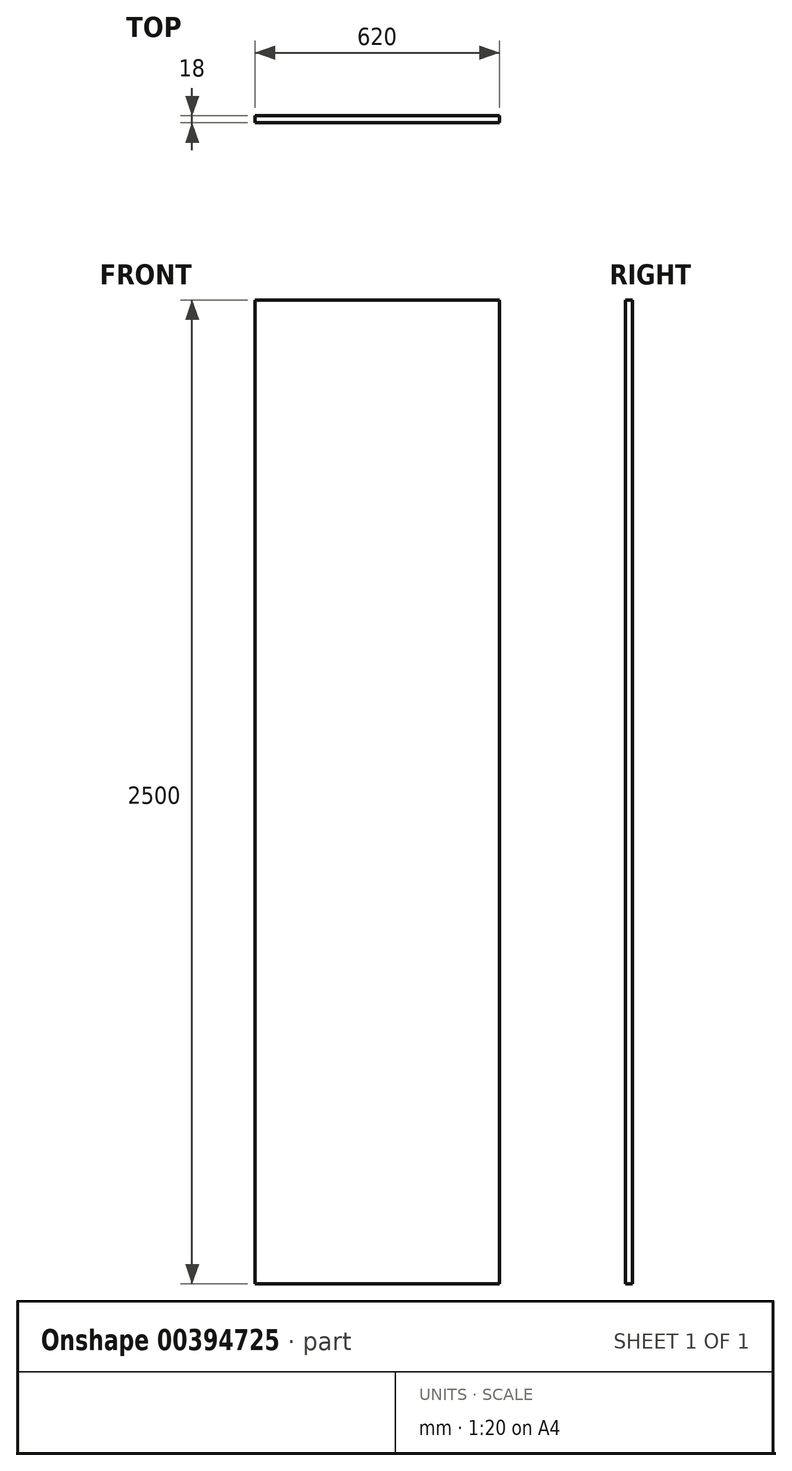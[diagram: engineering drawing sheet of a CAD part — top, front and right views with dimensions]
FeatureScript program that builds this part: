
annotation { "Feature Type Name" : "Feature", "Feature Type Description" : "" }
export const myFeature = defineFeature(function(context is Context, id is Id, definition is map)
    precondition{}
    {
        {
            var Q0;
            Q0=qCreatedBy(makeId("Front.planeOp"),FACE);
            var sketch = newSketch(context, id + "F0", { "sketchPlane" : qUnion([Q0])});
            skLineSegment(sketch, "E0.bottom", {"start": v(-26.85, 2454.82) * mm, "end": v(593.15, 2454.82) * mm});
            skLineSegment(sketch, "E0.top", {"start": v(-26.85, -45.18) * mm, "end": v(593.15, -45.18) * mm});
            skLineSegment(sketch, "E0.left", {"start": v(-26.85, 2454.82) * mm, "end": v(-26.85, -45.18) * mm});
            skLineSegment(sketch, "E0.right", {"start": v(593.15, 2454.82) * mm, "end": v(593.15, -45.18) * mm});
            skSolve(sketch);
        }
        {
            var Q0;
            Q0=makeQuery(id+"F0.imprint","IMPRINT",FACE,{"disambiguationData":[TD([[makeQuery(id+"F0.imprint","IMPRINT",EDGE,{"derivedFrom":sQuery(id+"F0.wireOp",EDGE,"E0.bottom")}),-1.0]])]});
            extrude(context, id + "F1", {"entities" : qUnion([Q0]), "depth" : 18 * mm});
        }
    });
